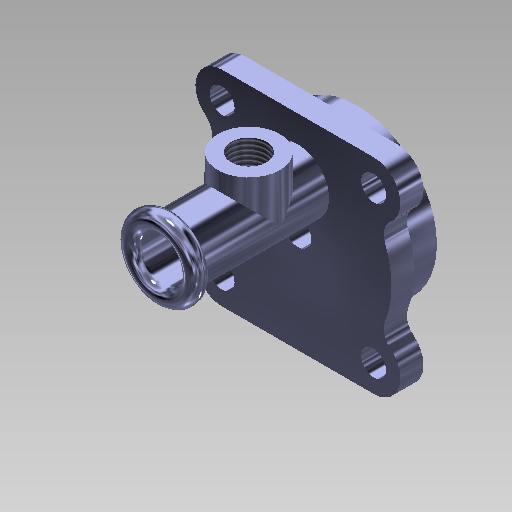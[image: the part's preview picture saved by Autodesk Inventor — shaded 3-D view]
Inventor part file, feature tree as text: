
AUTODESK INVENTOR PART (.ipt)
format: ipt  version: 2018.1 (Build 221171000, 171)  size: 256,512 bytes
history: native  units: in
note: dims shown in document units (in); Inventor stores cm internally (conversion verified against a paired STEP export)
features: sketch x9, extrude x8, plane x2, revolve x1, thread x1
ambient origin geometry x8: Origin, YZ Plane, XZ Plane, XY Plane, X Axis, Y Axis, Z Axis, Center Point
bodies: Solid1 (feature_tree)
feature tree (21):
  extrude  "Extrusion1"  Depth=0.1024in TaperAngle=0.0deg
  extrude  "Extrusion2"  Depth=0.5906in TaperAngle=0.0deg
  extrude  "Extrusion3"  TaperAngle=90.0deg  [1 undecoded]
  extrude  "Extrusion4"  Depth=0.0787in TaperAngle=0.0deg
  plane  "Work Plane1"
  revolve  "Revolution1"  [1 undecoded]
  plane  "Work Plane2"
  extrude  "Extrusion6"  Depth=0.3937in TaperAngle=0.0deg
  extrude  "Extrusion8"  [1 undecoded]
  extrude  "Extrusion9"  [1 undecoded]
  thread  "Thread1"  [1 undecoded]
  extrude  "Extrusion10"  [1 undecoded]
  sketch  "Sketch1"  dims[d0=0.1024in d1=0.0in d3=0.1575in d4=0.0in]
  sketch  "Sketch2"  dims[d10=0.1575in d11=0.0in d13=0.5906in d14=0.0in]
  sketch  "Sketch3"  dims[d18=0.3346in d22=90.0deg]
  sketch  "Sketch4"  dims[d23=0.7874in d26=0.0787in d27=0.1378in d28=0.0in d29=0.0in]
  sketch  "Sketch6"  dims[d32=0.7874in d33=0.0in d35=0.1969in d36=0.0in]
  sketch  "Sketch7"  dims[d37=0.3937in d38=0.0in d40=0.3937in d41=0.0in]
  sketch  "Sketch8"
  sketch  "Sketch9"
  sketch  "Sketch10"
note: 6 required parameter values undecoded (feature->parameter linkage not recoverable at this tier; creation-order binding heuristic only, values carry confidence <= 0.55)